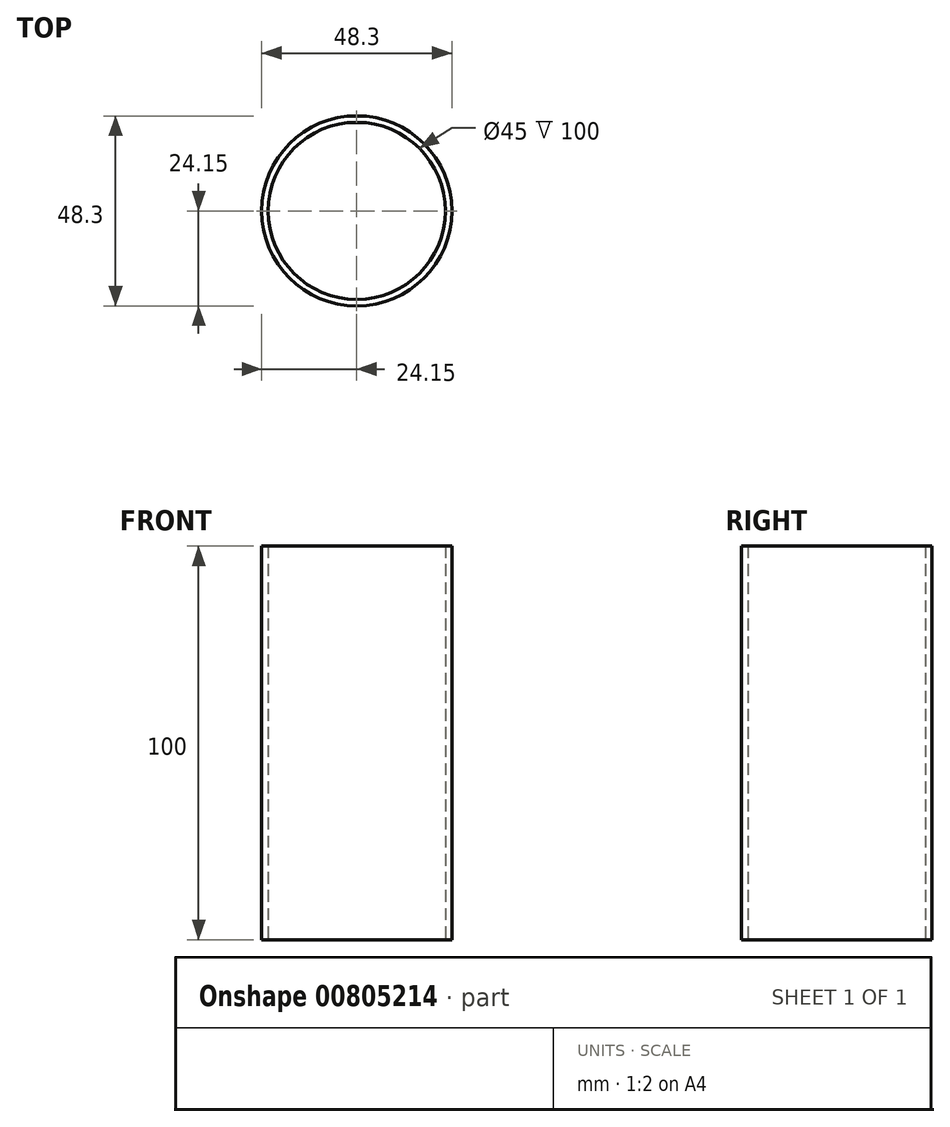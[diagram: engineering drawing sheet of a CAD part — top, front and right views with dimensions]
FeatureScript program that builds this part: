
annotation { "Feature Type Name" : "Feature", "Feature Type Description" : "" }
export const myFeature = defineFeature(function(context is Context, id is Id, definition is map)
    precondition{}
    {
        {
            var Q0;
            Q0=qCreatedBy(makeId("Top.planeOp"),FACE);
            var sketch = newSketch(context, id + "F0", { "sketchPlane" : qUnion([Q0])});
            skCircle(sketch, "E0", {"center": v(0, 0) * mm, "radius": 24.15 * mm});
            skCircle(sketch, "E1", {"center": v(0, 0) * mm, "radius": 22.5 * mm});
            skSolve(sketch);
        }
        {
            var Q0;
            Q0=makeQuery(id+"F0.imprint","IMPRINT",FACE,{"disambiguationData":[TD([[makeQuery(id+"F0.imprint","IMPRINT",EDGE,{"derivedFrom":sQuery(id+"F0.wireOp",EDGE,"E0")}),1.0]])]});
            var sketch = newSketch(context, id + "F1", { "sketchPlane" : qUnion([Q0])});
            skSolve(sketch);
        }
        {
            var Q0;
            Q0=makeQuery(id+"F1.imprint","IMPRINT",FACE,{"disambiguationData":[TD([[makeQuery(id+"F1.imprint","IMPRINT",EDGE,{"derivedFrom":makeQuery(id+"F0.imprint","IMPRINT",EDGE,{"derivedFrom":sQuery(id+"F0.wireOp",EDGE,"E0")})}),1.0]])]});
            extrude(context, id + "F2", {"entities" : qUnion([Q0]), "depth" : 100 * mm, "offsetDistance" : 25 * mm});
        }
    });
